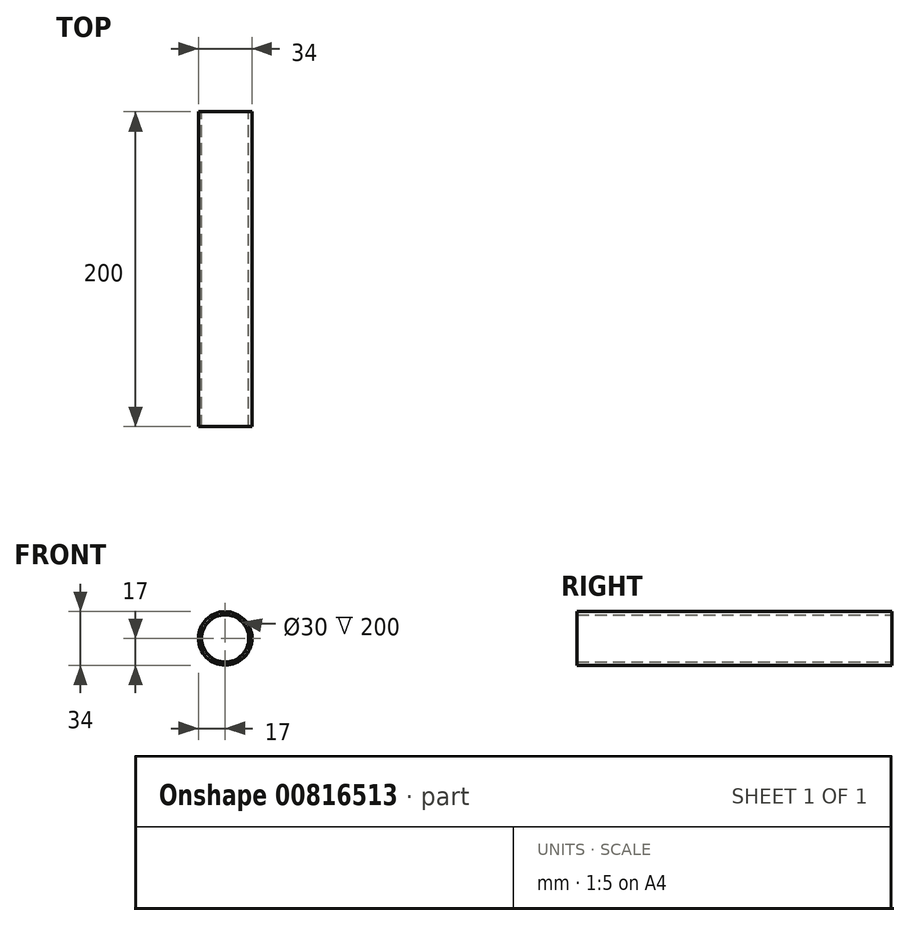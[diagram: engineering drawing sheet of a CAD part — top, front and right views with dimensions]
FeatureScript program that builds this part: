
annotation { "Feature Type Name" : "Feature", "Feature Type Description" : "" }
export const myFeature = defineFeature(function(context is Context, id is Id, definition is map)
    precondition{}
    {
        {
            var Q0;
            Q0=qCreatedBy(makeId("Front.planeOp"),FACE);
            var sketch = newSketch(context, id + "F0", { "sketchPlane" : qUnion([Q0])});
            skCircle(sketch, "E0", {"center": v(0, 0) * mm, "radius": 17 * mm});
            skCircle(sketch, "E1", {"center": v(0, 0) * mm, "radius": 15 * mm});
            skSolve(sketch);
        }
        {
            var Q0;
            Q0=makeQuery(id+"F0.imprint","IMPRINT",FACE,{"disambiguationData":[TD([[makeQuery(id+"F0.imprint","IMPRINT",EDGE,{"derivedFrom":sQuery(id+"F0.wireOp",EDGE,"E0")}),1.0]])]});
            extrude(context, id + "F1", {"entities" : qUnion([Q0]), "depth" : 200 * mm, "offsetDistance" : 25 * mm});
        }
    });
